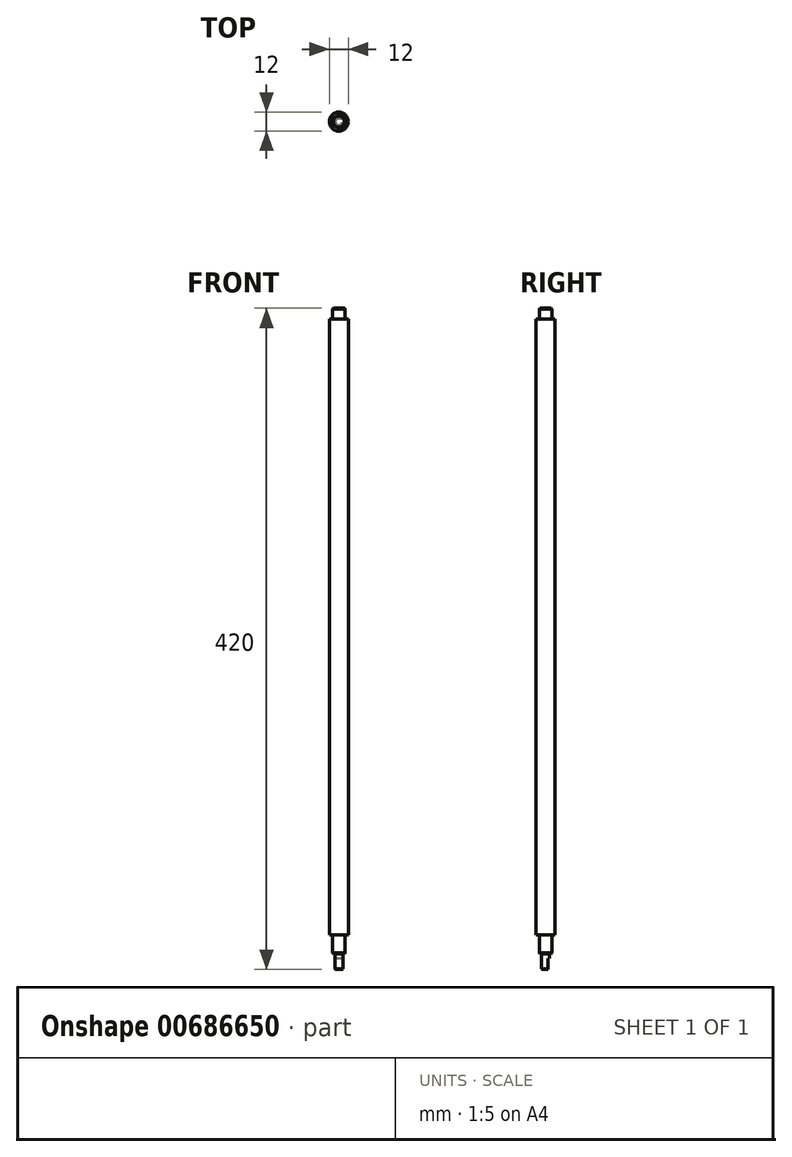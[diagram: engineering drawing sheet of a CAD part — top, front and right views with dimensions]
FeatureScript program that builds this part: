
annotation { "Feature Type Name" : "Feature", "Feature Type Description" : "" }
export const myFeature = defineFeature(function(context is Context, id is Id, definition is map)
    precondition{}
    {
        {
            var Q0;
            Q0=qCreatedBy(makeId("Top.planeOp"),FACE);
            var sketch = newSketch(context, id + "F0", { "sketchPlane" : qUnion([Q0])});
            skCircle(sketch, "E0", {"center": v(0, 0) * mm, "radius": 4 * mm});
            skSolve(sketch);
        }
        {
            var Q0;
            Q0 = qSketchRegion(id + "F0", true);
            extrude(context, id + "F1", {"entities" : qUnion([Q0]), "oppositeDirection" : true, "depth" : 7 * mm, "offsetDistance" : 25 * mm});
        }
        {
            var Q0;
            Q0=makeQuery(id+"F1.opExtrude","CAP_EDGE",EDGE,{"disambiguationData":[OSD([sQuery(id+"F0.wireOp",EDGE,"E0")])],"isStart":true});
            chamfer(context, id + "F2", {"entities" : qUnion([Q0]), "width" : 0.5 * mm, "tangentPropagation" : true});
        }
        {
            var Q0;
            Q0=makeQuery(id+"F1.opExtrude","CAP_FACE",FACE,{"disambiguationData":[OSD([sQuery(id+"F0.wireOp",EDGE,"E0")])],"isStart":false});
            var sketch = newSketch(context, id + "F3", { "sketchPlane" : qUnion([Q0])});
            skCircle(sketch, "E1", {"center": v(0, 0) * mm, "radius": 6 * mm});
            skSolve(sketch);
        }
        {
            var Q0;
            Q0 = qSketchRegion(id + "F3", true);
            extrude(context, id + "F4", {"entities" : qUnion([Q0]), "operationType" : NewBodyOperationType.ADD, "depth" : 391 * mm, "offsetDistance" : 25 * mm});
        }
        {
            var Q0;
            Q0=makeQuery(id+"F4.opExtrude","CAP_FACE",FACE,{"disambiguationData":[OSD([sQuery(id+"F3.wireOp",EDGE,"E1")])],"isStart":false});
            var sketch = newSketch(context, id + "F5", { "sketchPlane" : qUnion([Q0])});
            skCircle(sketch, "E2", {"center": v(0, 0) * mm, "radius": 4 * mm});
            skSolve(sketch);
        }
        {
            var Q0;
            Q0 = qSketchRegion(id + "F5", true);
            extrude(context, id + "F6", {"entities" : qUnion([Q0]), "operationType" : NewBodyOperationType.ADD, "depth" : 12 * mm, "offsetDistance" : 25 * mm});
        }
        {
            var Q0;
            Q0=makeQuery(id+"F6.opExtrude","CAP_EDGE",EDGE,{"disambiguationData":[OSD([sQuery(id+"F5.wireOp",EDGE,"E2")])],"isStart":false});
            chamfer(context, id + "F7", {"entities" : qUnion([Q0]), "width" : 0.5 * mm, "tangentPropagation" : true});
        }
        {
            var Q0;
            Q0=makeQuery(id+"F6.opExtrude","CAP_FACE",FACE,{"disambiguationData":[OSD([sQuery(id+"F5.wireOp",EDGE,"E2")])],"isStart":false});
            var sketch = newSketch(context, id + "F8", { "sketchPlane" : qUnion([Q0])});
            skCircle(sketch, "E3", {"center": v(0, 0) * mm, "radius": 2.5 * mm});
            skSolve(sketch);
        }
        {
            var Q0;
            Q0 = qSketchRegion(id + "F8", true);
            extrude(context, id + "F9", {"entities" : qUnion([Q0]), "operationType" : NewBodyOperationType.ADD, "depth" : 10 * mm, "offsetDistance" : 25 * mm});
        }
        {
            var Q0;
            Q0=makeQuery(id+"F9.opExtrude","CAP_EDGE",EDGE,{"disambiguationData":[OSD([sQuery(id+"F8.wireOp",EDGE,"E3")])],"isStart":false});
            chamfer(context, id + "F10", {"entities" : qUnion([Q0]), "width" : 0.5 * mm, "tangentPropagation" : true});
        }
        {
            var Q0;
            Q0=makeQuery(id+"F9.opExtrude","CAP_FACE",FACE,{"disambiguationData":[OSD([sQuery(id+"F8.wireOp",EDGE,"E3")])],"isStart":false});
            var sketch = newSketch(context, id + "F11", { "sketchPlane" : qUnion([Q0])});
            skCircle(sketch, "E4.0", {"center": v(0, 0) * mm, "radius": 2.5 * mm});
            skPoint(sketch, "E5", {"position": v(0, -2.5) * mm});
            skLineSegment(sketch, "E6.bottom", {"start": v(2, -1.5) * mm, "end": v(-2, -1.5) * mm});
            skLineSegment(sketch, "E6.top", {"start": v(2, -3.5) * mm, "end": v(-2, -3.5) * mm, "construction": true});
            skLineSegment(sketch, "E6.left", {"start": v(2, -1.5) * mm, "end": v(2, -3.5) * mm, "construction": true});
            skLineSegment(sketch, "E6.right", {"start": v(-2, -1.5) * mm, "end": v(-2, -3.5) * mm, "construction": true});
            skSolve(sketch);
        }
        {
            var Q0;
            {var subQ0=sQuery(id+"F11.wireOp",EDGE,"E6.bottom");var subQ1=sQuery(id+"F8.wireOp",EDGE,"E3");var subQ2=makeQuery(id+"F10.opChamfer","BLEND_EDGE",EDGE,{"blendedFrom":[makeQuery(id+"F9.opExtrude","CAP_EDGE",EDGE,{"disambiguationData":[OSD([subQ1])],"isStart":false}),makeQuery(id+"F9.opExtrude","CAP_FACE",FACE,{"disambiguationData":[OSD([subQ1])],"isStart":false})],"blendedInto":[makeQuery(id+"F9.opExtrude","CAP_FACE",FACE,{"disambiguationData":[OSD([subQ1])],"isStart":false})]});var subQ3=makeQuery(id+"F11.imprint","INTERSECT",VERTEX,{"disambiguationData":[OD(0.0)],"derivedFrom":[subQ2,subQ0]});Q0=makeQuery(id+"F11.imprint","IMPRINT",FACE,{"disambiguationData":[TD([[makeQuery(id+"F11.imprint","IMPRINT",EDGE,{"disambiguationData":[TD([[subQ3,-1.0]])],"derivedFrom":subQ0}),1.0]])]});}
            var Q1;
            {var subQ0=sQuery(id+"F11.wireOp",EDGE,"E6.bottom");var subQ1=sQuery(id+"F11.wireOp",EDGE,"E4.0");var subQ2=makeQuery(id+"F11.imprint","INTERSECT",VERTEX,{"disambiguationData":[OD(0.0)],"derivedFrom":[subQ1,subQ0]});Q1=makeQuery(id+"F11.imprint","IMPRINT",FACE,{"disambiguationData":[TD([[makeQuery(id+"F11.imprint","IMPRINT",EDGE,{"disambiguationData":[TD([[subQ2,1.0]])],"derivedFrom":subQ1}),1.0]])]});}
            extrude(context, id + "F12", {"entities" : qUnion([Q0, Q1]), "operationType" : NewBodyOperationType.REMOVE, "oppositeDirection" : true, "depth" : 7 * mm, "offsetDistance" : 25 * mm});
        }
    });
